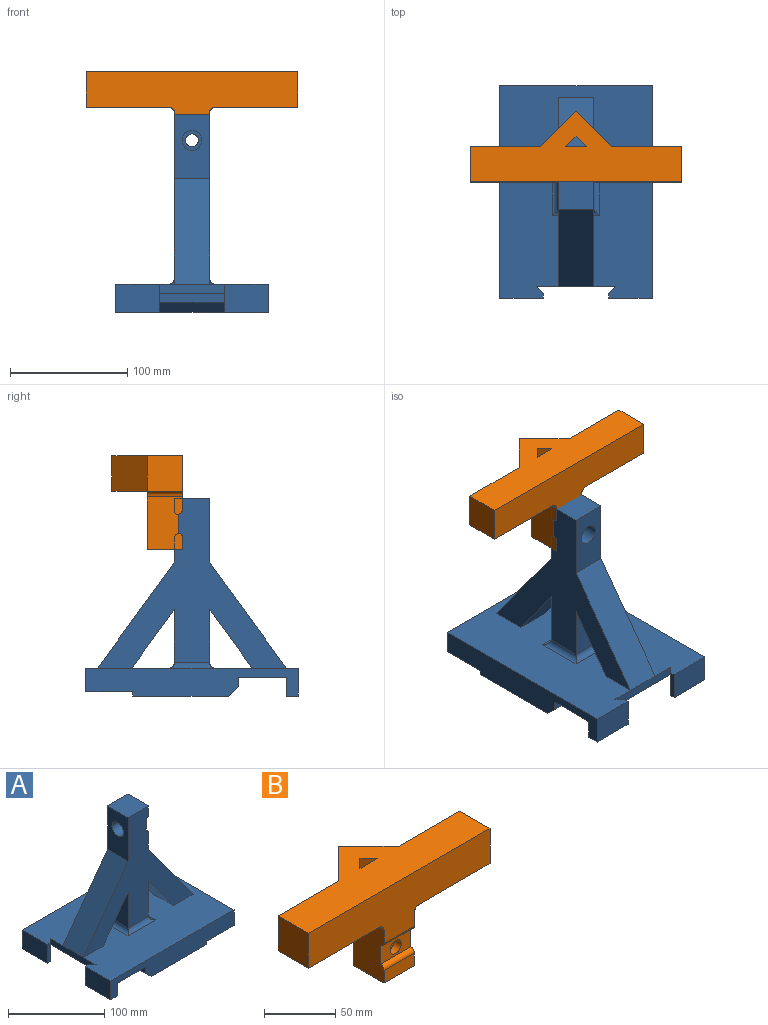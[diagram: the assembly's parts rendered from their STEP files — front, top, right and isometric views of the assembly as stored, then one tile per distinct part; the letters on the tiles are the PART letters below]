
ASSEMBLY  parts=2 mates=1
PART A: 43 faces, bbox 181.1x130x168.8 mm
  f0: cylinder r=5.5mm len=11mm, axis (1,0,0), area 300.7mm2, adj f30,f38
  f1: plane 181.12x130mm, normal (0,0,1), area 19606.8mm2, adj f5,f8,f13,f14,f19,f20,f21,f22
  f2: plane 45x30mm, normal (1,0,0), area 1350mm2, adj f5,f27,f35,f42
  f3: plane 45x30mm, normal (-1,0,0), area 1350mm2, adj f5,f27,f34,f39
  f4: plane 30x10.81mm, normal (1,0,0), area 324.2mm2, adj f5,f27,f29,f32
  f5: plane 161.12x145mm, normal (0,1,0), area 8220.9mm2, adj f1,f2,f3,f4,f26,f28,f29,f30
  f6: plane 31.28x16.26mm, normal (1,0,0), area 508.5mm2, adj f7,f16,f20,f24
  f7: plane 37.28x10mm, normal (0,0,-1), area 354.7mm2, adj f6,f14,f20,f23,f24
  f8: plane 37.28x23.84mm, normal (-1,0,0), area 888.6mm2, adj f1,f9,f19,f21
  f9: plane 37.28x10mm, normal (0,0,-1), area 354.7mm2, adj f8,f15,f19,f21,f25
  f10: plane 130x81.42mm, normal (0,0,-1), area 10584mm2, adj f11,f18,f19,f20
  f11: plane 130x3.84mm, normal (1,0,0), area 499.2mm2, adj f10,f12,f19,f20
  f12: plane 130x40mm, normal (0,0,-1), area 5200mm2, adj f11,f13,f19,f20
  f13: plane 130x20mm, normal (1,0,0), area 2600mm2, adj f1,f12,f19,f20
  f14: plane 37.28x23.84mm, normal (-1,0,0), area 888.6mm2, adj f1,f7,f20,f23
  f15: plane 31.28x16.26mm, normal (1,0,0), area 508.5mm2, adj f9,f16,f19,f25
  f16: plane 130x41mm, normal (0,0,-1), area 5330mm2, adj f6,f15,f17,f19,f20,f22
  f17: plane 130x8mm, normal (-1,0,0), area 1040mm2, adj f16,f18,f19,f20
  f18: plane 130x8.7mm, normal (-0.69,0,-0.73), area 1560mm2, adj f10,f17,f19,f20
  f19: plane 181.12x23.84mm, normal (0,-1,0), area 3461.7mm2, adj f1,f8,f9,f10,f11,f12,f13,f15
  f20: plane 181.12x23.84mm, normal (0,1,0), area 3461.7mm2, adj f1,f6,f7,f10,f11,f12,f13,f14
  f21: plane 23.84x4mm, normal (0,1,0), area 95.4mm2, adj f1,f8,f9,f25
  f22: plane 67.45x7.58mm, normal (-1,0,0), area 511.3mm2, adj f1,f16,f24,f25,f33
  f23: plane 23.84x4mm, normal (0,-1,0), area 95.4mm2, adj f1,f7,f14,f24
  f24: plane 23.84x6mm, normal (0.71,-0.71,0), area 202.3mm2, adj f1,f6,f7,f22,f23
  f25: plane 23.84x6mm, normal (0.71,0.71,0), area 202.3mm2, adj f1,f9,f15,f21,f22
  f26: plane 55x30mm, normal (-1,0,0), area 1423mm2, adj f5,f27,f29,f33,f37
  f27: plane 161.12x145mm, normal (0,-1,0), area 8220.9mm2, adj f1,f2,f3,f4,f26,f28,f29,f30
  f28: plane 30x21.11mm, normal (1,0,0), area 633.2mm2, adj f5,f27,f31,f36
  f29: plane 30x30mm, normal (0,0,1), area 900mm2, adj f4,f5,f26,f27
  f30: plane 30x16.1mm, normal (1,0,0), area 388mm2, adj f0,f5,f27,f31,f32
  f31: cylinder r=3.5mm len=30mm, axis (0,1,0), area 158.9mm2, adj f5,f27,f28,f30
  f32: cylinder r=3.5mm len=30mm, axis (0,1,0), area 158.9mm2, adj f4,f5,f27,f30
  f33: plane 90x65.56mm, normal (-0.81,0,0.59), area 3340.4mm2, adj f5,f22,f26,f27
  f34: plane 50x36.42mm, normal (0.81,0,-0.59), area 1855.8mm2, adj f1,f3,f5,f27
  f35: plane 50x36.42mm, normal (-0.81,0,-0.59), area 1855.8mm2, adj f1,f2,f5,f27
  f36: plane 90x65.56mm, normal (0.81,0,0.59), area 3340.4mm2, adj f1,f5,f27,f28
  f37: cylinder r=8.5mm len=18mm, axis (-1,0,0), area 961.3mm2, adj f26,f38
  f38: plane 17x17mm, normal (-1,0,0), area 131.9mm2, adj f0,f37
  f39: cylinder r=5mm len=40mm, axis (0,1,0), area 264.2mm2, adj f1,f3,f40,f41
  f40: cylinder r=5mm len=40mm, axis (-1,0,0), area 264.2mm2, adj f1,f27,f39,f42
  f41: cylinder r=5mm len=40mm, axis (1,0,0), area 264.2mm2, adj f1,f5,f39,f42
  f42: cylinder r=5mm len=40mm, axis (0,-1,0), area 264.2mm2, adj f1,f2,f40,f41
PART B: 24 faces, bbox 180x60x80 mm
  f0: plane 60x30mm, normal (0,1,0), area 1800mm2, adj f2,f3,f17,f23
  f1: plane 180x46.1mm, normal (0,-1,0), area 5893.7mm2, adj f2,f3,f8,f9,f13,f20,f21,f22
  f2: plane 180x60mm, normal (0,0,1), area 6222.8mm2, adj f0,f1,f4,f5,f16,f17,f18,f19
  f3: plane 180x60mm, normal (0,0,-1), area 5022.8mm2, adj f0,f1,f4,f5,f16,f17,f18,f19
  f4: plane 80x40mm, normal (0,1,0), area 1811mm2, adj f2,f3,f8,f9,f10,f15,f18,f19
  f5: plane 60x30mm, normal (0,1,0), area 1800mm2, adj f2,f3,f16,f22
  f6: cylinder r=5.5mm len=11mm, axis (0,-1,0), area 226mm2, adj f11,f14
  f7: plane 30x10.8mm, normal (0,-1,0), area 324mm2, adj f8,f9,f10,f12
  f8: plane 45x30mm, normal (1,0,0), area 1289mm2, adj f1,f4,f7,f10,f11,f12,f13,f21
  f9: plane 45x30mm, normal (-1,0,0), area 1289mm2, adj f1,f4,f7,f10,f11,f12,f13,f20
  f10: plane 30x30mm, normal (0,0,-1), area 900mm2, adj f4,f7,f8,f9
  f11: plane 30x16.1mm, normal (0,-1,0), area 388mm2, adj f6,f8,f9,f12,f13
  f12: cylinder r=3.5mm len=30mm, axis (-1,0,0), area 163.7mm2, adj f7,f8,f9,f11
  f13: cylinder r=3.5mm len=30mm, axis (-1,0,0), area 163.7mm2, adj f1,f8,f9,f11
  f14: plane 17x17mm, normal (0,1,0), area 131.9mm2, adj f6,f15
  f15: cylinder r=8.5mm len=20mm, axis (0,1,0), area 1068.1mm2, adj f4,f14
  f16: plane 30x30mm, normal (0.71,0.71,0), area 1272.8mm2, adj f2,f3,f5,f17
  f17: plane 30x30mm, normal (-0.71,0.71,0), area 1272.8mm2, adj f0,f2,f3,f16
  f18: plane 30x8.79mm, normal (0.71,-0.71,0), area 372.8mm2, adj f2,f3,f4,f19
  f19: plane 30x8.79mm, normal (-0.71,-0.71,0), area 372.8mm2, adj f2,f3,f4,f18
  f20: cylinder r=5mm len=30mm, axis (0,1,0), area 235.6mm2, adj f1,f3,f4,f9
  f21: cylinder r=5mm len=30mm, axis (0,-1,0), area 235.6mm2, adj f1,f3,f4,f8
  f22: plane 30x30mm, normal (1,0,0), area 900mm2, adj f1,f2,f3,f5
  f23: plane 30x30mm, normal (-1,0,0), area 900mm2, adj f0,f1,f2,f3
PLACE A rot(axis=(0,0,1),90deg) t=(-10.78,-157.63,-60.84)mm
PLACE B t=(54.22,-153.26,40.15)mm
MATE parallel A.f37 <-> B.f6  axis (0,1,0) through (54.22,-164.8,61.81)mm
